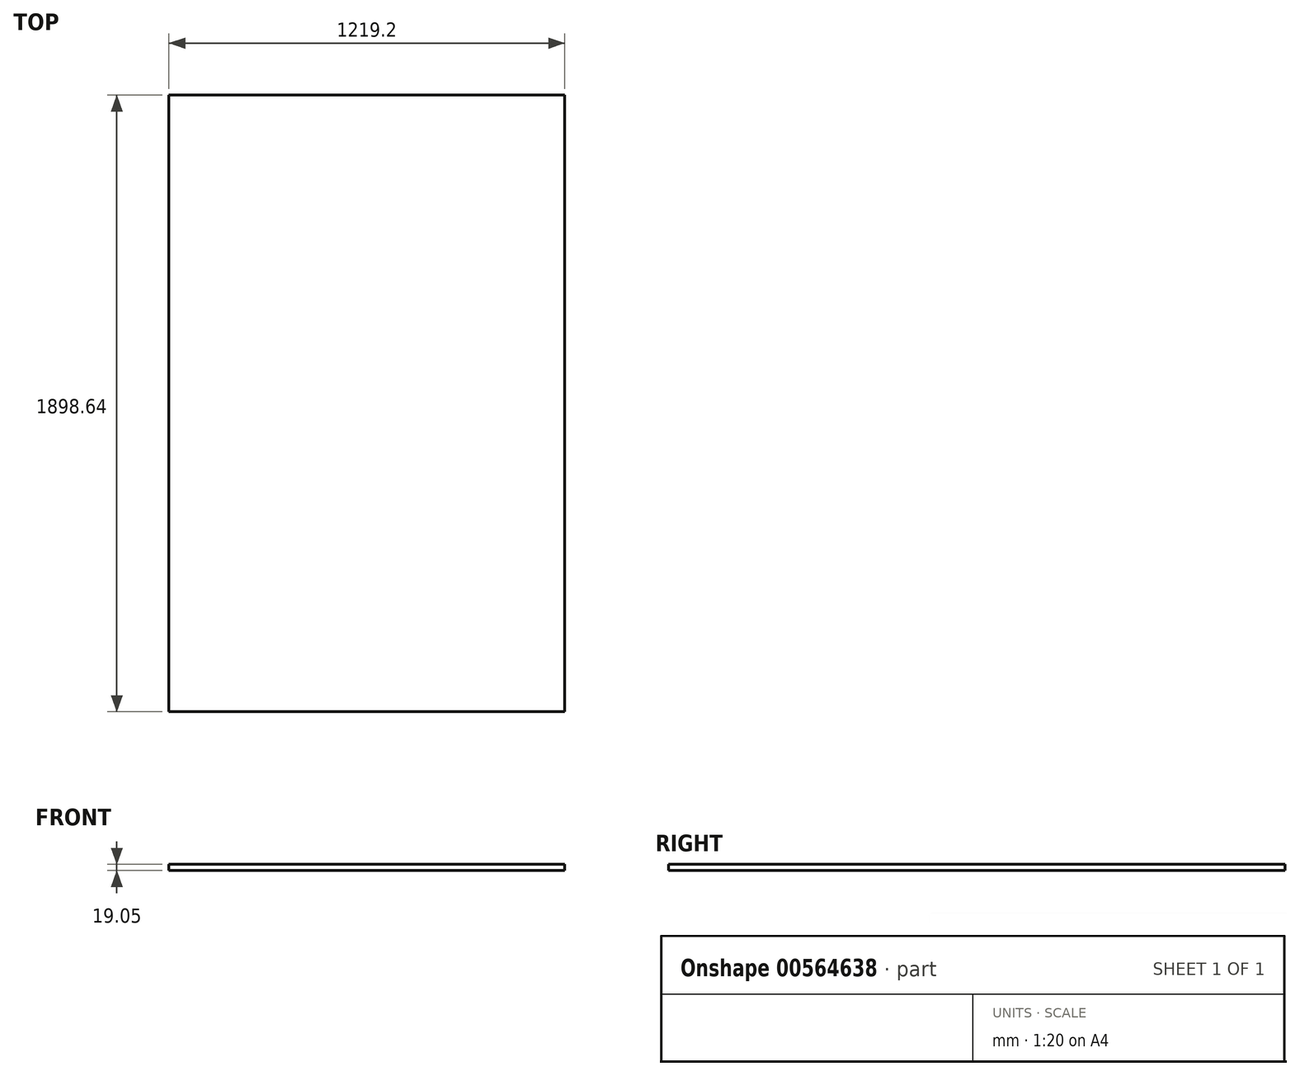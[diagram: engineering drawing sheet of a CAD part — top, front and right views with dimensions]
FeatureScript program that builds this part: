
annotation { "Feature Type Name" : "Feature", "Feature Type Description" : "" }
export const myFeature = defineFeature(function(context is Context, id is Id, definition is map)
    precondition{}
    {
        {
            var Q0;
            Q0=qCreatedBy(makeId("Top.planeOp"),FACE);
            var sketch = newSketch(context, id + "F0", { "sketchPlane" : qUnion([Q0])});
            skLineSegment(sketch, "E0.bottom", {"start": v(-609.6, 949.32) * mm, "end": v(609.6, 949.32) * mm});
            skLineSegment(sketch, "E0.top", {"start": v(-609.6, -949.32) * mm, "end": v(609.6, -949.32) * mm});
            skLineSegment(sketch, "E0.left", {"start": v(-609.6, 949.32) * mm, "end": v(-609.6, -949.32) * mm});
            skLineSegment(sketch, "E0.right", {"start": v(609.6, 949.32) * mm, "end": v(609.6, -949.32) * mm});
            skPoint(sketch, "E0.middle", {"position": v(0, 0) * mm});
            skSolve(sketch);
        }
        {
            var Q0;
            Q0=makeQuery(id+"F0.imprint","IMPRINT",FACE,{"disambiguationData":[TD([[makeQuery(id+"F0.imprint","IMPRINT",EDGE,{"derivedFrom":sQuery(id+"F0.wireOp",EDGE,"E0.bottom")}),-1.0]])]});
            extrude(context, id + "F1", {"entities" : qUnion([Q0]), "depth" : 19.05 * mm, "offsetDistance" : 25.4 * mm});
        }
    });
